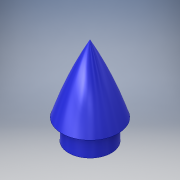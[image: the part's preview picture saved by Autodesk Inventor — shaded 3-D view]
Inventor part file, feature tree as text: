
AUTODESK INVENTOR PART (.ipt)
format: ipt  version: 2018 (Build 220112000, 112)  size: 132,608 bytes
history: native  units: in
note: dims shown in document units (in); Inventor stores cm internally (conversion verified against a paired STEP export)
features: revolve x1, sketch x1
ambient origin geometry x8: Origin, YZ Plane, XZ Plane, XY Plane, X Axis, Y Axis, Z Axis, Center Point
bodies: Solid1 (feature_tree)
feature tree (2):
  revolve  "Revolution1"  [1 undecoded]
  sketch  "Sketch1"  dims[d0=1.5625in d1=5.0in d3=14.0in d4=90.0deg d5=1.5in d6=1.5in d7=2.5in d9=0.75in d10=0.25in d11=0.75in d12=0.25in]
note: 1 required parameter value undecoded (feature->parameter linkage not recoverable at this tier; creation-order binding heuristic only, values carry confidence <= 0.55)
